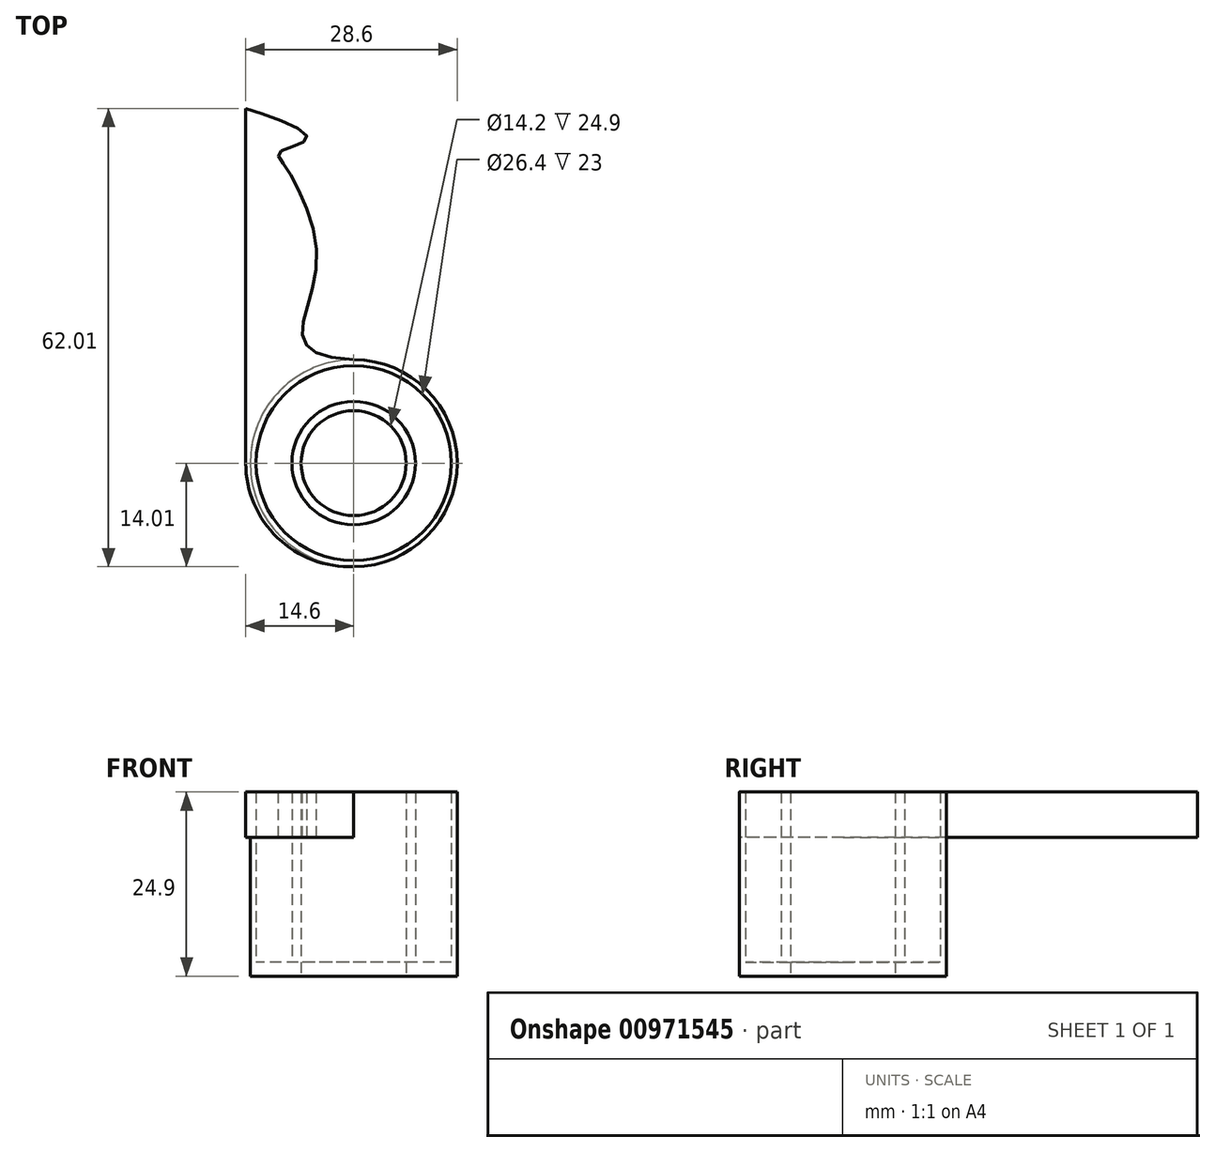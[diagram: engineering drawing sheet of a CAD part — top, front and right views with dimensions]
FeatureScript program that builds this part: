
annotation { "Feature Type Name" : "Feature", "Feature Type Description" : "" }
export const myFeature = defineFeature(function(context is Context, id is Id, definition is map)
    precondition{}
    {
        {
            var Q0;
            Q0=qCreatedBy(makeId("Top.planeOp"),FACE);
            var sketch = newSketch(context, id + "F0", { "sketchPlane" : qUnion([Q0])});
            skCircle(sketch, "E0", {"center": v(0, 0) * mm, "radius": 7.1 * mm});
            skCircle(sketch, "E1", {"center": v(0, 0) * mm, "radius": 14 * mm});
            skSolve(sketch);
        }
        {
            var Q0;
            Q0=makeQuery(id+"F0.imprint","IMPRINT",FACE,{"disambiguationData":[TD([[makeQuery(id+"F0.imprint","IMPRINT",EDGE,{"derivedFrom":sQuery(id+"F0.wireOp",EDGE,"E0")}),-1.0]])]});
            extrude(context, id + "F1", {"entities" : qUnion([Q0]), "depth" : 1.9 * mm, "offsetDistance" : 25 * mm});
        }
        {
            var Q0;
            Q0=makeQuery(id+"F1.opExtrude","CAP_FACE",FACE,{"disambiguationData":[OSD([sQuery(id+"F0.wireOp",EDGE,"E0"),sQuery(id+"F0.wireOp",EDGE,"E1")])],"isStart":false});
            var sketch = newSketch(context, id + "F2", { "sketchPlane" : qUnion([Q0])});
            skPoint(sketch, "E2.0", {"position": v(0, 0) * mm});
            skCircle(sketch, "E3", {"center": v(0, 0) * mm, "radius": 8.35 * mm});
            skCircle(sketch, "E4.0", {"center": v(0, 0) * mm, "radius": 7.1 * mm});
            skCircle(sketch, "E5", {"center": v(0, 0) * mm, "radius": 13.2 * mm});
            skCircle(sketch, "E6.0", {"center": v(0, 0) * mm, "radius": 14 * mm});
            skSolve(sketch);
        }
        {
            var Q0;
            Q0=makeQuery(id+"F2.imprint","IMPRINT",FACE,{"disambiguationData":[TD([[makeQuery(id+"F2.imprint","IMPRINT",EDGE,{"derivedFrom":sQuery(id+"F2.wireOp",EDGE,"E3")}),1.0]])]});
            var Q1;
            Q1=makeQuery(id+"F2.imprint","IMPRINT",FACE,{"disambiguationData":[TD([[makeQuery(id+"F2.imprint","IMPRINT",EDGE,{"derivedFrom":sQuery(id+"F2.wireOp",EDGE,"E5")}),-1.0]])]});
            extrude(context, id + "F3", {"entities" : qUnion([Q0, Q1]), "operationType" : NewBodyOperationType.ADD, "depth" : 23 * mm, "offsetDistance" : 25 * mm});
        }
        {
            var Q0;
            Q0=makeQuery(id+"F3.opExtrude","CAP_FACE",FACE,{"disambiguationData":[OSD([sQuery(id+"F2.wireOp",EDGE,"E5"),sQuery(id+"F2.wireOp",EDGE,"E6.0")])],"isStart":false});
            var sketch = newSketch(context, id + "F4", { "sketchPlane" : qUnion([Q0])});
            skLineSegment(sketch, "E7", {"start": v(0, 0) * mm, "end": v(0, -14) * mm, "construction": true});
            skLineSegment(sketch, "E8", {"start": v(0, 0) * mm, "end": v(0, 14) * mm, "construction": true});
            skLineSegment(sketch, "E9", {"start": v(0, 0) * mm, "end": v(-14, 0) * mm, "construction": true});
            skLineSegment(sketch, "E10", {"start": v(-14, 0) * mm, "end": v(-14.6, 0) * mm, "construction": true});
            skArc(sketch, "E11", {"start": v(0, 14) * mm, "mid": v(-14.6, 0) * mm, "end": v(0, -14) * mm});
            skLineSegment(sketch, "E12", {"start": v(-14.6, 0) * mm, "end": v(-14.6, -48) * mm});
            skLineSegment(sketch, "E13", {"start": v(-14.6, -44) * mm, "end": v(-6.3, -44) * mm, "construction": true});
            skLineSegment(sketch, "E14", {"start": v(-14.6, -42.1) * mm, "end": v(-10, -42.1) * mm, "construction": true});
            skLineSegment(sketch, "E15", {"start": v(-14.6, -27.9) * mm, "end": v(-5, -27.9) * mm, "construction": true});
            skLineSegment(sketch, "E16", {"start": v(-14.6, -17.3) * mm, "end": v(-6.9, -17.3) * mm, "construction": true});
            skFitSpline(sketch, "E17", {"points": [v(-14.6, -48) * mm, v(-6.3, -44) * mm, v(-10, -42.1) * mm, v(-9.38, -40.32) * mm, v(-5, -27.9) * mm, v(-6.9, -17.3) * mm, v(0, -14) * mm], "startDerivative": vector(42.28, 12.16) * mm, "endDerivative": vector(78.7, 3.3) * mm});
            skLineSegment(sketch, "E18", {"start": v(0, -14) * mm, "end": v(-3.88, -14.16) * mm, "construction": true});
            skLineSegment(sketch, "E19", {"start": v(-14.6, -48) * mm, "end": v(-6.42, -48) * mm, "construction": true});
            skLineSegment(sketch, "E20", {"start": v(-14.6, -48) * mm, "end": v(-8.57, -46.27) * mm, "construction": true});
            skLineSegment(sketch, "E21", {"start": v(0, 14) * mm, "end": v(-9.89, 0) * mm});
            skLineSegment(sketch, "E22", {"start": v(-9.89, 0) * mm, "end": v(0, -14) * mm});
            skLineSegment(sketch, "E23.MirrorCS", {"start": v(-14.6, 0) * mm, "end": v(-14.6, 48) * mm});
            skFitSpline(sketch, "E24.MirrorCS", {"points": [v(-14.6, 48) * mm, v(-6.3, 44) * mm, v(-10, 42.1) * mm, v(-9.38, 40.32) * mm, v(-5, 27.9) * mm, v(-6.9, 17.3) * mm, v(0, 14) * mm], "startDerivative": vector(42.28, -12.16) * mm, "endDerivative": vector(78.7, -3.3) * mm});
            skLineSegment(sketch, "E25.MirrorCS", {"start": v(-14.6, 27.9) * mm, "end": v(-5, 27.9) * mm, "construction": true});
            skLineSegment(sketch, "E26.MirrorCS", {"start": v(-14.6, 44) * mm, "end": v(-6.3, 44) * mm, "construction": true});
            skLineSegment(sketch, "E27.MirrorCS", {"start": v(-14.6, 48) * mm, "end": v(-8.57, 46.27) * mm, "construction": true});
            skLineSegment(sketch, "E28.MirrorCS", {"start": v(-14.6, 48) * mm, "end": v(-6.42, 48) * mm, "construction": true});
            skSolve(sketch);
        }
        {
            var Q0;
            {var subQ2=sQuery(id+"F4.wireOp",EDGE,"E23.MirrorCS");Q0=makeQuery(id+"F4.imprint","IMPRINT",FACE,{"disambiguationData":[TD([[makeQuery(id+"F4.imprint","IMPRINT",EDGE,{"derivedFrom":subQ2}),-1.0]])]});}
            var Q1;
            {var subQ0=sQuery(id+"F4.wireOp",EDGE,"E11");var subQ3=makeQuery(id+"F4.imprint","INTERSECT",VERTEX,{"derivedFrom":[subQ0,sQuery(id+"F4.wireOp",EDGE,"E12"),sQuery(id+"F4.wireOp",EDGE,"E23.MirrorCS")]});Q1=makeQuery(id+"F4.imprint","IMPRINT",FACE,{"disambiguationData":[TD([[makeQuery(id+"F4.imprint","IMPRINT",EDGE,{"disambiguationData":[TD([[subQ3,1.0]])],"derivedFrom":subQ0}),1.0]])]});}
            extrude(context, id + "F5", {"entities" : qUnion([Q0, Q1]), "operationType" : NewBodyOperationType.ADD, "oppositeDirection" : true, "depth" : 6.1 * mm, "offsetDistance" : 25 * mm});
        }
    });
